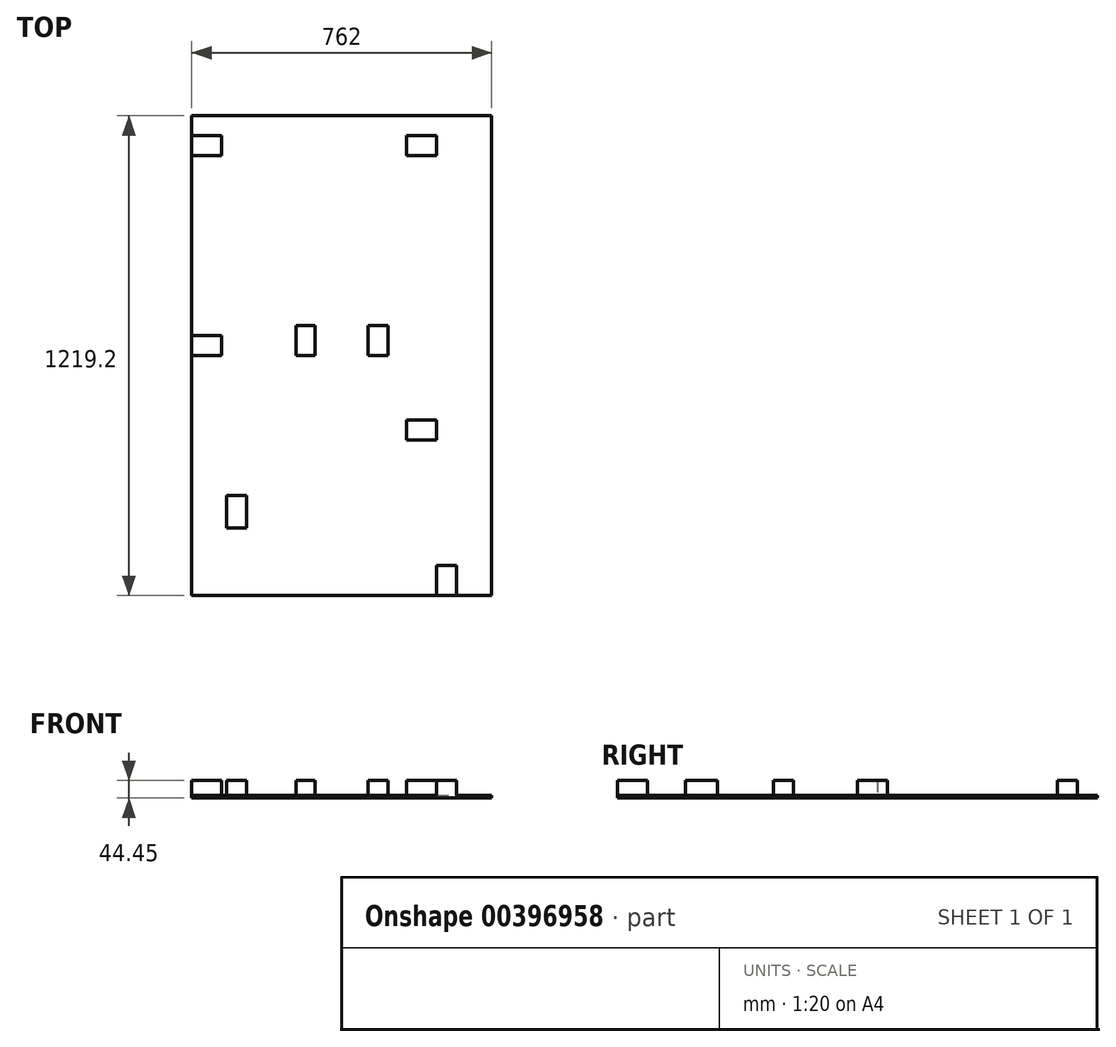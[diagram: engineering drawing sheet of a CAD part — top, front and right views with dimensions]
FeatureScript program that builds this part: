
annotation { "Feature Type Name" : "Feature", "Feature Type Description" : "" }
export const myFeature = defineFeature(function(context is Context, id is Id, definition is map)
    precondition{}
    {
        {
            var Q0;
            Q0=qCreatedBy(makeId("Top.planeOp"),FACE);
            var sketch = newSketch(context, id + "F0", { "sketchPlane" : qUnion([Q0])});
            skLineSegment(sketch, "E0.bottom", {"start": v(381, -685.8) * mm, "end": v(-381, -685.8) * mm});
            skLineSegment(sketch, "E0.top", {"start": v(381, 533.4) * mm, "end": v(-381, 533.4) * mm});
            skLineSegment(sketch, "E0.left", {"start": v(381, -685.8) * mm, "end": v(381, 533.4) * mm});
            skLineSegment(sketch, "E0.right", {"start": v(-381, -685.8) * mm, "end": v(-381, 533.4) * mm});
            skPoint(sketch, "E0.middle", {"position": v(0, -76.2) * mm});
            skSolve(sketch);
        }
        {
            var Q0;
            Q0 = qSketchRegion(id + "F0", true);
            extrude(context, id + "F1", {"entities" : qUnion([Q0]), "oppositeDirection" : true, "depth" : 6.35 * mm});
        }
        {
            var Q0;
            Q0=makeQuery(id+"F1.opExtrude","CAP_FACE",FACE,{"disambiguationData":[OSD([sQuery(id+"F0.wireOp",EDGE,"E0.bottom"),sQuery(id+"F0.wireOp",EDGE,"E0.top"),sQuery(id+"F0.wireOp",EDGE,"E0.left"),sQuery(id+"F0.wireOp",EDGE,"E0.right")])],"isStart":true});
            var sketch = newSketch(context, id + "F2", { "sketchPlane" : qUnion([Q0])});
            skLineSegment(sketch, "E1.bottom", {"start": v(-381, 431.8) * mm, "end": v(-304.8, 431.8) * mm});
            skLineSegment(sketch, "E1.top", {"start": v(-381, 482.6) * mm, "end": v(-304.8, 482.6) * mm});
            skLineSegment(sketch, "E1.left", {"start": v(-381, 431.8) * mm, "end": v(-381, 482.6) * mm});
            skLineSegment(sketch, "E1.right", {"start": v(-304.8, 431.8) * mm, "end": v(-304.8, 482.6) * mm});
            skLineSegment(sketch, "E2.bottom", {"start": v(165.1, 482.6) * mm, "end": v(241.3, 482.6) * mm});
            skLineSegment(sketch, "E2.top", {"start": v(165.1, 431.8) * mm, "end": v(241.3, 431.8) * mm});
            skLineSegment(sketch, "E2.left", {"start": v(165.1, 482.6) * mm, "end": v(165.1, 431.8) * mm});
            skLineSegment(sketch, "E2.right", {"start": v(241.3, 482.6) * mm, "end": v(241.3, 431.8) * mm});
            skLineSegment(sketch, "E3.bottom", {"start": v(165.1, -239.16) * mm, "end": v(241.3, -239.16) * mm});
            skLineSegment(sketch, "E3.top", {"start": v(165.1, -289.96) * mm, "end": v(241.3, -289.96) * mm});
            skLineSegment(sketch, "E3.left", {"start": v(165.1, -239.16) * mm, "end": v(165.1, -289.96) * mm});
            skLineSegment(sketch, "E3.right", {"start": v(241.3, -239.16) * mm, "end": v(241.3, -289.96) * mm});
            skLineSegment(sketch, "E4.bottom", {"start": v(66.1, 0) * mm, "end": v(116.9, 0) * mm});
            skLineSegment(sketch, "E5.bottom", {"start": v(-292.1, -431.8) * mm, "end": v(-241.3, -431.8) * mm});
            skLineSegment(sketch, "E5.top", {"start": v(-292.1, -431.8) * mm, "end": v(-241.3, -431.8) * mm});
            skLineSegment(sketch, "E5.left", {"start": v(-292.1, -431.8) * mm, "end": v(-292.1, -431.8) * mm});
            skLineSegment(sketch, "E5.right", {"start": v(-241.3, -431.8) * mm, "end": v(-241.3, -431.8) * mm});
            skLineSegment(sketch, "E6.bottom", {"start": v(241.3, -685.8) * mm, "end": v(292.1, -685.8) * mm});
            skLineSegment(sketch, "E6.top", {"start": v(241.3, -609.6) * mm, "end": v(292.1, -609.6) * mm});
            skLineSegment(sketch, "E6.left", {"start": v(241.3, -685.8) * mm, "end": v(241.3, -609.6) * mm});
            skLineSegment(sketch, "E6.right", {"start": v(292.1, -685.8) * mm, "end": v(292.1, -609.6) * mm});
            skLineSegment(sketch, "E7", {"start": v(381, -609.6) * mm, "end": v(-381, -609.6) * mm});
            skLineSegment(sketch, "E8.bottom", {"start": v(-381, -76.2) * mm, "end": v(-304.8, -76.2) * mm});
            skLineSegment(sketch, "E8.top", {"start": v(-381, -25.4) * mm, "end": v(-304.8, -25.4) * mm});
            skLineSegment(sketch, "E8.left", {"start": v(-381, -76.2) * mm, "end": v(-381, -25.4) * mm});
            skLineSegment(sketch, "E8.right", {"start": v(-304.8, -76.2) * mm, "end": v(-304.8, -25.4) * mm});
            skLineSegment(sketch, "E9.top", {"start": v(-292.1, -513.42) * mm, "end": v(-241.3, -513.42) * mm});
            skLineSegment(sketch, "E9.left", {"start": v(-292.1, -431.8) * mm, "end": v(-292.1, -513.42) * mm});
            skLineSegment(sketch, "E9.right", {"start": v(-241.3, -431.8) * mm, "end": v(-241.3, -513.42) * mm});
            skLineSegment(sketch, "E10.top", {"start": v(-116.58, -76.2) * mm, "end": v(-68.19, -76.2) * mm});
            skLineSegment(sketch, "E10.left", {"start": v(-116.58, 0) * mm, "end": v(-116.58, -76.2) * mm});
            skLineSegment(sketch, "E10.right", {"start": v(-68.19, 0) * mm, "end": v(-68.19, -76.2) * mm});
            skLineSegment(sketch, "E11.top", {"start": v(66.1, -76.2) * mm, "end": v(116.9, -76.2) * mm});
            skLineSegment(sketch, "E11.left", {"start": v(66.1, 0) * mm, "end": v(66.1, -76.2) * mm});
            skLineSegment(sketch, "E11.right", {"start": v(116.9, 0) * mm, "end": v(116.9, -76.2) * mm});
            skLineSegment(sketch, "E12", {"start": v(-68.19, 0) * mm, "end": v(-116.58, 0) * mm});
            skSolve(sketch);
        }
        {
            var Q0;
            Q0 = qSketchRegion(id + "F2", true);
            extrude(context, id + "F3", {"entities" : qUnion([Q0]), "operationType" : NewBodyOperationType.ADD, "depth" : 38.1 * mm});
        }
    });
